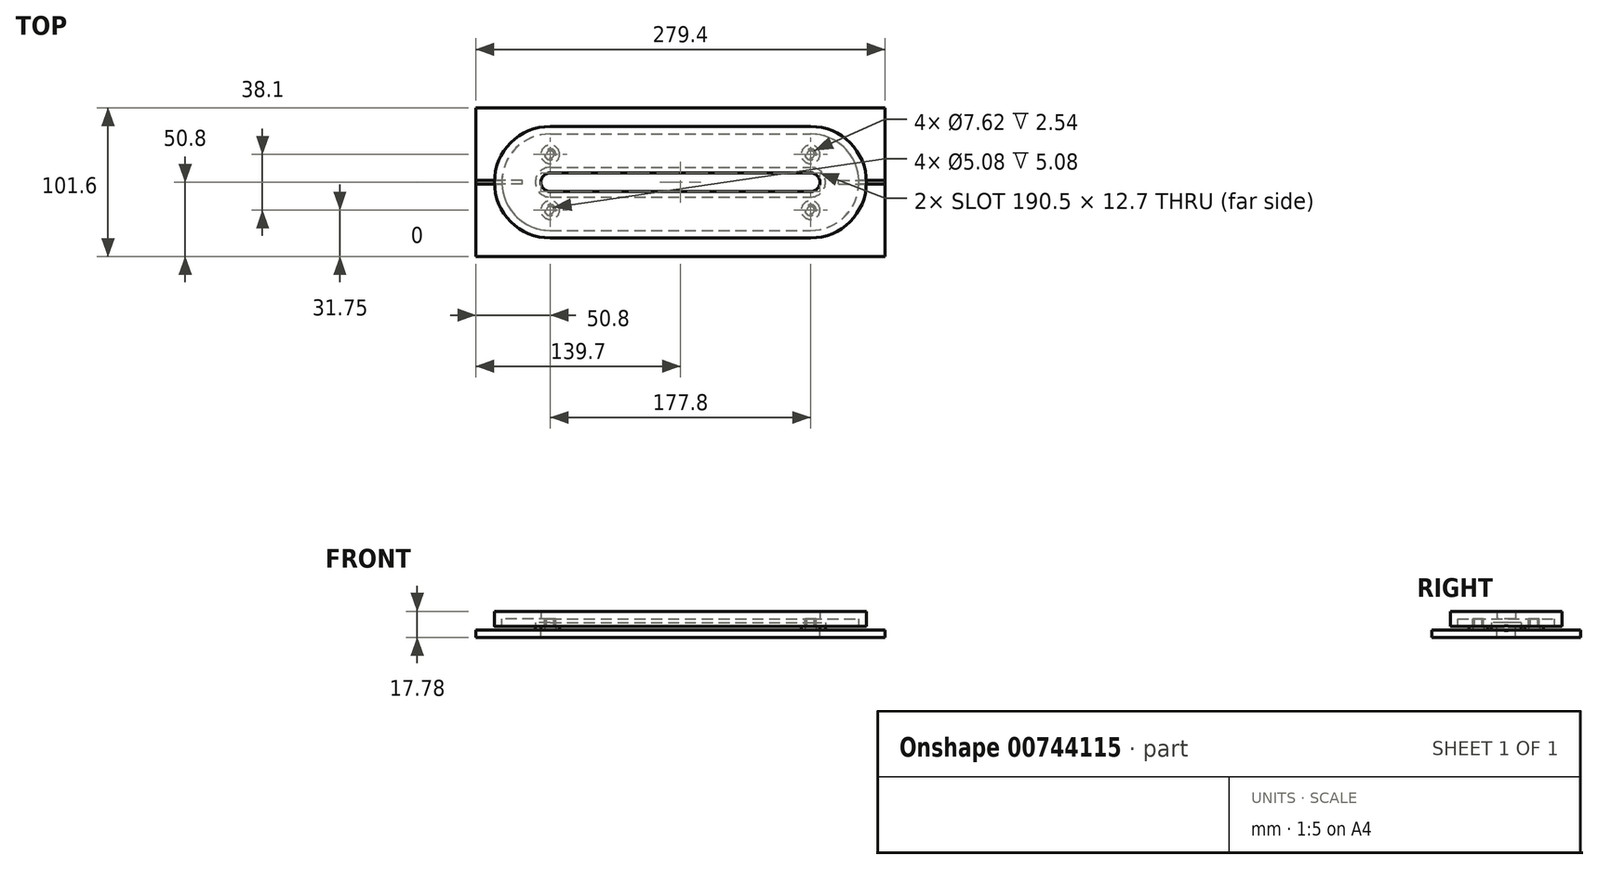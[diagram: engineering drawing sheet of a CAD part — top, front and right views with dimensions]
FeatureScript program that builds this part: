
annotation { "Feature Type Name" : "Feature", "Feature Type Description" : "" }
export const myFeature = defineFeature(function(context is Context, id is Id, definition is map)
    precondition{}
    {
        {
            var Q0;
            Q0=qCreatedBy(makeId("Top.planeOp"),FACE);
            var sketch = newSketch(context, id + "F0", { "sketchPlane" : qUnion([Q0])});
            skLineSegment(sketch, "E0.bottom", {"start": v(-139.7, 50.8) * mm, "end": v(139.7, 50.8) * mm});
            skLineSegment(sketch, "E0.top", {"start": v(-139.7, -50.8) * mm, "end": v(139.7, -50.8) * mm});
            skLineSegment(sketch, "E0.left", {"start": v(-139.7, 50.8) * mm, "end": v(-139.7, -50.8) * mm});
            skLineSegment(sketch, "E0.right", {"start": v(139.7, 50.8) * mm, "end": v(139.7, -50.8) * mm});
            skPoint(sketch, "E0.middle", {"position": v(0, 0) * mm});
            skSolve(sketch);
        }
        {
            var Q0;
            Q0 = qSketchRegion(id + "F0", true);
            extrude(context, id + "F1", {"entities" : qUnion([Q0]), "depth" : 5.08 * mm, "offsetDistance" : 25.4 * mm});
        }
        {
            var Q0;
            Q0=makeQuery(id+"F1.opExtrude","CAP_FACE",FACE,{"disambiguationData":[OSD([sQuery(id+"F0.wireOp",EDGE,"E0.bottom"),sQuery(id+"F0.wireOp",EDGE,"E0.top"),sQuery(id+"F0.wireOp",EDGE,"E0.left"),sQuery(id+"F0.wireOp",EDGE,"E0.right")])],"isStart":false});
            var sketch = newSketch(context, id + "F2", { "sketchPlane" : qUnion([Q0])});
            skLineSegment(sketch, "E1", {"start": v(-139.7, 0) * mm, "end": v(139.7, 0) * mm, "construction": true});
            skLineSegment(sketch, "E2.bottom", {"start": v(-88.9, -6.35) * mm, "end": v(88.9, -6.35) * mm});
            skLineSegment(sketch, "E2.top", {"start": v(-88.9, 6.35) * mm, "end": v(88.9, 6.35) * mm});
            skLineSegment(sketch, "E2.left", {"start": v(-88.9, -6.35) * mm, "end": v(-88.9, 6.35) * mm, "construction": true});
            skLineSegment(sketch, "E2.right", {"start": v(88.9, -6.35) * mm, "end": v(88.9, 6.35) * mm, "construction": true});
            skPoint(sketch, "E2.middle", {"position": v(0, 0) * mm});
            skArc(sketch, "E3", {"start": v(-88.9, 6.35) * mm, "mid": v(-95.25, 0) * mm, "end": v(-88.9, -6.35) * mm});
            skArc(sketch, "E4", {"start": v(88.9, -6.35) * mm, "mid": v(95.25, 0) * mm, "end": v(88.9, 6.35) * mm});
            skSolve(sketch);
        }
        {
            var Q0;
            Q0 = qSketchRegion(id + "F2", true);
            extrude(context, id + "F3", {"entities" : qUnion([Q0]), "operationType" : NewBodyOperationType.REMOVE, "endBound" : BoundingType.THROUGH_ALL, "oppositeDirection" : true, "depth" : 25.4 * mm, "offsetDistance" : 25.4 * mm});
        }
        {
            var Q0;
            Q0=makeQuery(id+"F1.opExtrude","CAP_FACE",FACE,{"disambiguationData":[OSD([sQuery(id+"F0.wireOp",EDGE,"E0.bottom"),sQuery(id+"F0.wireOp",EDGE,"E0.top"),sQuery(id+"F0.wireOp",EDGE,"E0.left"),sQuery(id+"F0.wireOp",EDGE,"E0.right")])],"isStart":false});
            var sketch = newSketch(context, id + "F4", { "sketchPlane" : qUnion([Q0])});
            skLineSegment(sketch, "E5", {"start": v(-139.7, 0) * mm, "end": v(139.7, 0) * mm, "construction": true});
            skLineSegment(sketch, "E6.bottom", {"start": v(-88.9, 6.35) * mm, "end": v(88.9, 6.35) * mm});
            skLineSegment(sketch, "E6.top", {"start": v(-88.9, -6.35) * mm, "end": v(88.9, -6.35) * mm});
            skLineSegment(sketch, "E6.left", {"start": v(-88.9, 6.35) * mm, "end": v(-88.9, -6.35) * mm, "construction": true});
            skLineSegment(sketch, "E6.right", {"start": v(88.9, 6.35) * mm, "end": v(88.9, -6.35) * mm, "construction": true});
            skPoint(sketch, "E6.middle", {"position": v(0, 0) * mm});
            skArc(sketch, "E7", {"start": v(-88.9, 6.35) * mm, "mid": v(-95.25, 0) * mm, "end": v(-88.9, -6.35) * mm});
            skArc(sketch, "E8", {"start": v(88.9, -6.35) * mm, "mid": v(95.25, 0) * mm, "end": v(88.9, 6.35) * mm});
            skLineSegment(sketch, "E9.0", {"start": v(-88.9, 10.16) * mm, "end": v(88.9, 10.16) * mm});
            skArc(sketch, "E9.1", {"start": v(-88.9, 10.16) * mm, "mid": v(-99.06, 0) * mm, "end": v(-88.9, -10.16) * mm});
            skLineSegment(sketch, "E9.2", {"start": v(-88.9, -10.16) * mm, "end": v(88.9, -10.16) * mm});
            skArc(sketch, "E9.3", {"start": v(88.9, -10.16) * mm, "mid": v(99.06, 0) * mm, "end": v(88.9, 10.16) * mm});
            skSolve(sketch);
        }
        {
            var Q0;
            Q0 = qSketchRegion(id + "F4", true);
            extrude(context, id + "F5", {"entities" : qUnion([Q0]), "operationType" : NewBodyOperationType.ADD, "depth" : 5.08 * mm, "offsetDistance" : 25.4 * mm});
        }
        {
            var Q0;
            Q0=qCreatedBy(makeId("Top.planeOp"),FACE);
            cPlane(context, id + "F6", {"entities" : qUnion([Q0]), "cplaneType" : CPlaneType.OFFSET, "offset" : 12.7 * mm, "width" : 152.4 * mm, "height" : 152.4 * mm});
        }
        {
            var Q0;
            Q0=qCreatedBy(id+"F6.planeOp",FACE);
            var sketch = newSketch(context, id + "F7", { "sketchPlane" : qUnion([Q0])});
            skLineSegment(sketch, "E10.bottom", {"start": v(-88.9, 38.1) * mm, "end": v(88.9, 38.1) * mm});
            skLineSegment(sketch, "E10.top", {"start": v(-88.9, -38.1) * mm, "end": v(88.9, -38.1) * mm});
            skLineSegment(sketch, "E10.left", {"start": v(-88.9, 38.1) * mm, "end": v(-88.9, -38.1) * mm, "construction": true});
            skLineSegment(sketch, "E10.right", {"start": v(88.9, 38.1) * mm, "end": v(88.9, -38.1) * mm, "construction": true});
            skPoint(sketch, "E10.middle", {"position": v(0, 0) * mm});
            skLineSegment(sketch, "E11", {"start": v(-88.9, 0) * mm, "end": v(88.9, 0) * mm, "construction": true});
            skArc(sketch, "E12", {"start": v(-88.9, 38.1) * mm, "mid": v(-127, 0) * mm, "end": v(-88.9, -38.1) * mm});
            skArc(sketch, "E13", {"start": v(88.9, -38.1) * mm, "mid": v(127, 0) * mm, "end": v(88.9, 38.1) * mm});
            skLineSegment(sketch, "E14", {"start": v(-88.9, 6.35) * mm, "end": v(88.9, 6.35) * mm});
            skLineSegment(sketch, "E15", {"start": v(-88.9, -6.35) * mm, "end": v(88.9, -6.35) * mm});
            skLineSegment(sketch, "E16", {"start": v(0, 6.35) * mm, "end": v(0, -6.35) * mm, "construction": true});
            skArc(sketch, "E17", {"start": v(-88.9, 6.35) * mm, "mid": v(-95.25, 0) * mm, "end": v(-88.9, -6.35) * mm});
            skArc(sketch, "E18", {"start": v(88.9, -6.35) * mm, "mid": v(95.25, 0) * mm, "end": v(88.9, 6.35) * mm});
            skSolve(sketch);
        }
        {
            var Q0;
            Q0=makeQuery(id+"F7.imprint","IMPRINT",FACE,{"disambiguationData":[TD([[makeQuery(id+"F7.imprint","IMPRINT",EDGE,{"derivedFrom":sQuery(id+"F7.wireOp",EDGE,"E10.bottom")}),-1.0]])]});
            extrude(context, id + "F8", {"entities" : qUnion([Q0]), "depth" : 5.08 * mm, "offsetDistance" : 25.4 * mm});
        }
        {
            var Q0;
            Q0=makeQuery(id+"F8.opExtrude","CAP_FACE",FACE,{"disambiguationData":[OSD([sQuery(id+"F7.wireOp",EDGE,"E10.bottom"),sQuery(id+"F7.wireOp",EDGE,"E10.top"),sQuery(id+"F7.wireOp",EDGE,"E12"),sQuery(id+"F7.wireOp",EDGE,"E13"),sQuery(id+"F7.wireOp",EDGE,"E14"),sQuery(id+"F7.wireOp",EDGE,"E15"),sQuery(id+"F7.wireOp",EDGE,"E17"),sQuery(id+"F7.wireOp",EDGE,"E18")])],"isStart":true});
            var sketch = newSketch(context, id + "F9", { "sketchPlane" : qUnion([Q0])});
            skLineSegment(sketch, "E19.bottom", {"start": v(-88.9, 38.1) * mm, "end": v(88.9, 38.1) * mm});
            skLineSegment(sketch, "E19.top", {"start": v(-88.9, -38.1) * mm, "end": v(88.9, -38.1) * mm});
            skLineSegment(sketch, "E19.left", {"start": v(-88.9, 38.1) * mm, "end": v(-88.9, -38.1) * mm, "construction": true});
            skLineSegment(sketch, "E19.right", {"start": v(88.9, 38.1) * mm, "end": v(88.9, -38.1) * mm, "construction": true});
            skPoint(sketch, "E19.middle", {"position": v(0, 0) * mm});
            skArc(sketch, "E20", {"start": v(-88.9, 38.1) * mm, "mid": v(-127, 0) * mm, "end": v(-88.9, -38.1) * mm});
            skArc(sketch, "E21", {"start": v(88.9, -38.1) * mm, "mid": v(127, 0) * mm, "end": v(88.9, 38.1) * mm});
            skArc(sketch, "E22.0", {"start": v(-88.9, 33.02) * mm, "mid": v(-121.92, 0) * mm, "end": v(-88.9, -33.02) * mm});
            skLineSegment(sketch, "E22.1", {"start": v(-88.9, 33.02) * mm, "end": v(88.9, 33.02) * mm});
            skArc(sketch, "E22.2", {"start": v(88.9, -33.02) * mm, "mid": v(121.92, 0) * mm, "end": v(88.9, 33.02) * mm});
            skLineSegment(sketch, "E22.3", {"start": v(-88.9, -33.02) * mm, "end": v(88.9, -33.02) * mm});
            skSolve(sketch);
        }
        {
            var Q0;
            Q0=makeQuery(id+"F9.imprint","IMPRINT",FACE,{"disambiguationData":[TD([[makeQuery(id+"F9.imprint","IMPRINT",EDGE,{"derivedFrom":sQuery(id+"F9.wireOp",EDGE,"E19.bottom")}),-1.0]])]});
            extrude(context, id + "F10", {"entities" : qUnion([Q0]), "operationType" : NewBodyOperationType.ADD, "depth" : 5.08 * mm, "offsetDistance" : 25.4 * mm});
        }
        {
            var Q0;
            Q0=makeQuery(id+"F1.opExtrude","CAP_FACE",FACE,{"disambiguationData":[OSD([sQuery(id+"F0.wireOp",EDGE,"E0.bottom"),sQuery(id+"F0.wireOp",EDGE,"E0.top"),sQuery(id+"F0.wireOp",EDGE,"E0.left"),sQuery(id+"F0.wireOp",EDGE,"E0.right")])],"isStart":false});
            var sketch = newSketch(context, id + "F11", { "sketchPlane" : qUnion([Q0])});
            skLineSegment(sketch, "E23", {"start": v(-139.7, 0) * mm, "end": v(139.7, 0) * mm, "construction": true});
            skLineSegment(sketch, "E24", {"start": v(0, 50.8) * mm, "end": v(0, -50.8) * mm, "construction": true});
            skCircle(sketch, "E25", {"center": v(-88.9, -19.05) * mm, "radius": 6.35 * mm});
            skCircle(sketch, "E26", {"center": v(-88.9, -19.05) * mm, "radius": 3.81 * mm});
            skCircle(sketch, "E27.MirrorC", {"center": v(-88.9, 19.05) * mm, "radius": 3.81 * mm});
            skCircle(sketch, "E28.MirrorC", {"center": v(-88.9, 19.05) * mm, "radius": 6.35 * mm});
            skCircle(sketch, "E29.MirrorC", {"center": v(88.9, -19.05) * mm, "radius": 3.81 * mm});
            skCircle(sketch, "E30.MirrorC", {"center": v(88.9, 19.05) * mm, "radius": 3.81 * mm});
            skCircle(sketch, "E31.MirrorC", {"center": v(88.9, -19.05) * mm, "radius": 6.35 * mm});
            skCircle(sketch, "E32.MirrorC", {"center": v(88.9, 19.05) * mm, "radius": 6.35 * mm});
            skSolve(sketch);
        }
        {
            var Q0;
            Q0 = qSketchRegion(id + "F11", true);
            extrude(context, id + "F12", {"entities" : qUnion([Q0]), "operationType" : NewBodyOperationType.ADD, "depth" : 2.54 * mm, "offsetDistance" : 25.4 * mm});
        }
        {
            var Q0;
            Q0=makeQuery(id+"F8.opExtrude","CAP_FACE",FACE,{"disambiguationData":[OSD([sQuery(id+"F7.wireOp",EDGE,"E10.bottom"),sQuery(id+"F7.wireOp",EDGE,"E10.top"),sQuery(id+"F7.wireOp",EDGE,"E12"),sQuery(id+"F7.wireOp",EDGE,"E13"),sQuery(id+"F7.wireOp",EDGE,"E14"),sQuery(id+"F7.wireOp",EDGE,"E15"),sQuery(id+"F7.wireOp",EDGE,"E17"),sQuery(id+"F7.wireOp",EDGE,"E18")])],"isStart":true});
            var sketch = newSketch(context, id + "F13", { "sketchPlane" : qUnion([Q0])});
            skLineSegment(sketch, "E33", {"start": v(-121.92, 0) * mm, "end": v(121.92, 0) * mm, "construction": true});
            skLineSegment(sketch, "E34", {"start": v(0, 33.02) * mm, "end": v(0, -33.02) * mm, "construction": true});
            skCircle(sketch, "E35", {"center": v(-88.9, -19.05) * mm, "radius": 3.68 * mm});
            skCircle(sketch, "E36", {"center": v(-88.9, -19.05) * mm, "radius": 2.54 * mm});
            skCircle(sketch, "E37.MirrorC", {"center": v(-88.9, 19.05) * mm, "radius": 2.54 * mm});
            skCircle(sketch, "E38.MirrorC", {"center": v(-88.9, 19.05) * mm, "radius": 3.68 * mm});
            skCircle(sketch, "E39.MirrorC", {"center": v(88.9, -19.05) * mm, "radius": 3.68 * mm});
            skCircle(sketch, "E40.MirrorC", {"center": v(88.9, 19.05) * mm, "radius": 3.68 * mm});
            skCircle(sketch, "E41.MirrorC", {"center": v(88.9, 19.05) * mm, "radius": 2.54 * mm});
            skCircle(sketch, "E42.MirrorC", {"center": v(88.9, -19.05) * mm, "radius": 2.54 * mm});
            skSolve(sketch);
        }
        {
            var Q0;
            Q0 = qSketchRegion(id + "F13", true);
            extrude(context, id + "F14", {"entities" : qUnion([Q0]), "operationType" : NewBodyOperationType.ADD, "depth" : 5.08 * mm, "offsetDistance" : 25.4 * mm});
        }
        {
            var Q0;
            {var subQ0=sQuery(id+"F0.wireOp",EDGE,"E0.bottom");var subQ1=sQuery(id+"F0.wireOp",EDGE,"E0.right");var subQ2=sQuery(id+"F0.wireOp",EDGE,"E0.top");var subQ3=sQuery(id+"F0.wireOp",EDGE,"E0.left");Q0=makeQuery(id+"F12.boolean.opBoolean","SPLIT",FACE,{"disambiguationData":[TD([makeQuery(id+"F1.opExtrude","SWEPT_FACE",FACE,{"disambiguationData":[OSD([subQ0])]})])],"derivedFrom":makeQuery(id+"F1.opExtrude","CAP_FACE",FACE,{"disambiguationData":[OSD([subQ0,subQ2,subQ3,subQ1])],"isStart":false})});}
            var sketch = newSketch(context, id + "F15", { "sketchPlane" : qUnion([Q0])});
            skLineSegment(sketch, "E43", {"start": v(-139.7, 0) * mm, "end": v(139.7, 0) * mm, "construction": true});
            skLineSegment(sketch, "E44", {"start": v(0, 50.8) * mm, "end": v(0, -50.8) * mm, "construction": true});
            skLineSegment(sketch, "E45.bottom", {"start": v(-107.95, -1.27) * mm, "end": v(-139.7, -1.27) * mm});
            skLineSegment(sketch, "E45.top", {"start": v(-107.95, 1.27) * mm, "end": v(-139.7, 1.27) * mm});
            skLineSegment(sketch, "E45.left", {"start": v(-107.95, -1.27) * mm, "end": v(-107.95, 1.27) * mm});
            skLineSegment(sketch, "E45.right", {"start": v(-139.7, -1.27) * mm, "end": v(-139.7, 1.27) * mm});
            skPoint(sketch, "E45.middle", {"position": v(-123.83, 0) * mm});
            skLineSegment(sketch, "E46.MirrorCS", {"start": v(107.95, -1.27) * mm, "end": v(107.95, 1.27) * mm});
            skLineSegment(sketch, "E47.MirrorCS", {"start": v(139.7, -1.27) * mm, "end": v(139.7, 1.27) * mm});
            skPoint(sketch, "E48.MirrorP", {"position": v(123.83, 0) * mm});
            skLineSegment(sketch, "E49.MirrorCS", {"start": v(107.95, -1.27) * mm, "end": v(139.7, -1.27) * mm});
            skLineSegment(sketch, "E50.MirrorCS", {"start": v(107.95, 1.27) * mm, "end": v(139.7, 1.27) * mm});
            skSolve(sketch);
        }
        {
            var Q0;
            Q0 = qSketchRegion(id + "F15", true);
            extrude(context, id + "F16", {"entities" : qUnion([Q0]), "operationType" : NewBodyOperationType.REMOVE, "oppositeDirection" : true, "depth" : 0.25 * mm, "offsetDistance" : 25.4 * mm});
        }
        {
            var Q0;
            Q0=makeQuery(id+"F10.opExtrude","CAP_FACE",FACE,{"disambiguationData":[OSD([sQuery(id+"F9.wireOp",EDGE,"E19.bottom"),sQuery(id+"F9.wireOp",EDGE,"E19.top"),sQuery(id+"F9.wireOp",EDGE,"E20"),sQuery(id+"F9.wireOp",EDGE,"E21"),sQuery(id+"F9.wireOp",EDGE,"E22.0"),sQuery(id+"F9.wireOp",EDGE,"E22.1"),sQuery(id+"F9.wireOp",EDGE,"E22.2"),sQuery(id+"F9.wireOp",EDGE,"E22.3")])],"isStart":false});
            var sketch = newSketch(context, id + "F17", { "sketchPlane" : qUnion([Q0])});
            skLineSegment(sketch, "E51", {"start": v(-127, 0) * mm, "end": v(127, 0) * mm, "construction": true});
            skLineSegment(sketch, "E52", {"start": v(0, 38.1) * mm, "end": v(0, -38.1) * mm, "construction": true});
            skLineSegment(sketch, "E53.bottom", {"start": v(-127.63, 1.27) * mm, "end": v(-121.28, 1.27) * mm});
            skLineSegment(sketch, "E53.top", {"start": v(-127.63, -1.27) * mm, "end": v(-121.28, -1.27) * mm});
            skLineSegment(sketch, "E53.left", {"start": v(-127.63, 1.27) * mm, "end": v(-127.63, -1.27) * mm});
            skLineSegment(sketch, "E53.right", {"start": v(-121.28, 1.27) * mm, "end": v(-121.28, -1.27) * mm});
            skPoint(sketch, "E53.middle", {"position": v(-124.46, 0) * mm});
            skLineSegment(sketch, "E54.MirrorCS", {"start": v(121.28, 1.27) * mm, "end": v(121.28, -1.27) * mm});
            skLineSegment(sketch, "E55.MirrorCS", {"start": v(127.63, 1.27) * mm, "end": v(127.63, -1.27) * mm});
            skLineSegment(sketch, "E56.MirrorCS", {"start": v(127.63, 1.27) * mm, "end": v(121.28, 1.27) * mm});
            skLineSegment(sketch, "E57.MirrorCS", {"start": v(127.63, -1.27) * mm, "end": v(121.28, -1.27) * mm});
            skPoint(sketch, "E58.MirrorP", {"position": v(124.46, 0) * mm});
            skSolve(sketch);
        }
        {
            var Q0;
            Q0 = qSketchRegion(id + "F17", true);
            extrude(context, id + "F18", {"entities" : qUnion([Q0]), "operationType" : NewBodyOperationType.REMOVE, "oppositeDirection" : true, "depth" : 0.25 * mm, "offsetDistance" : 25.4 * mm});
        }
    });
